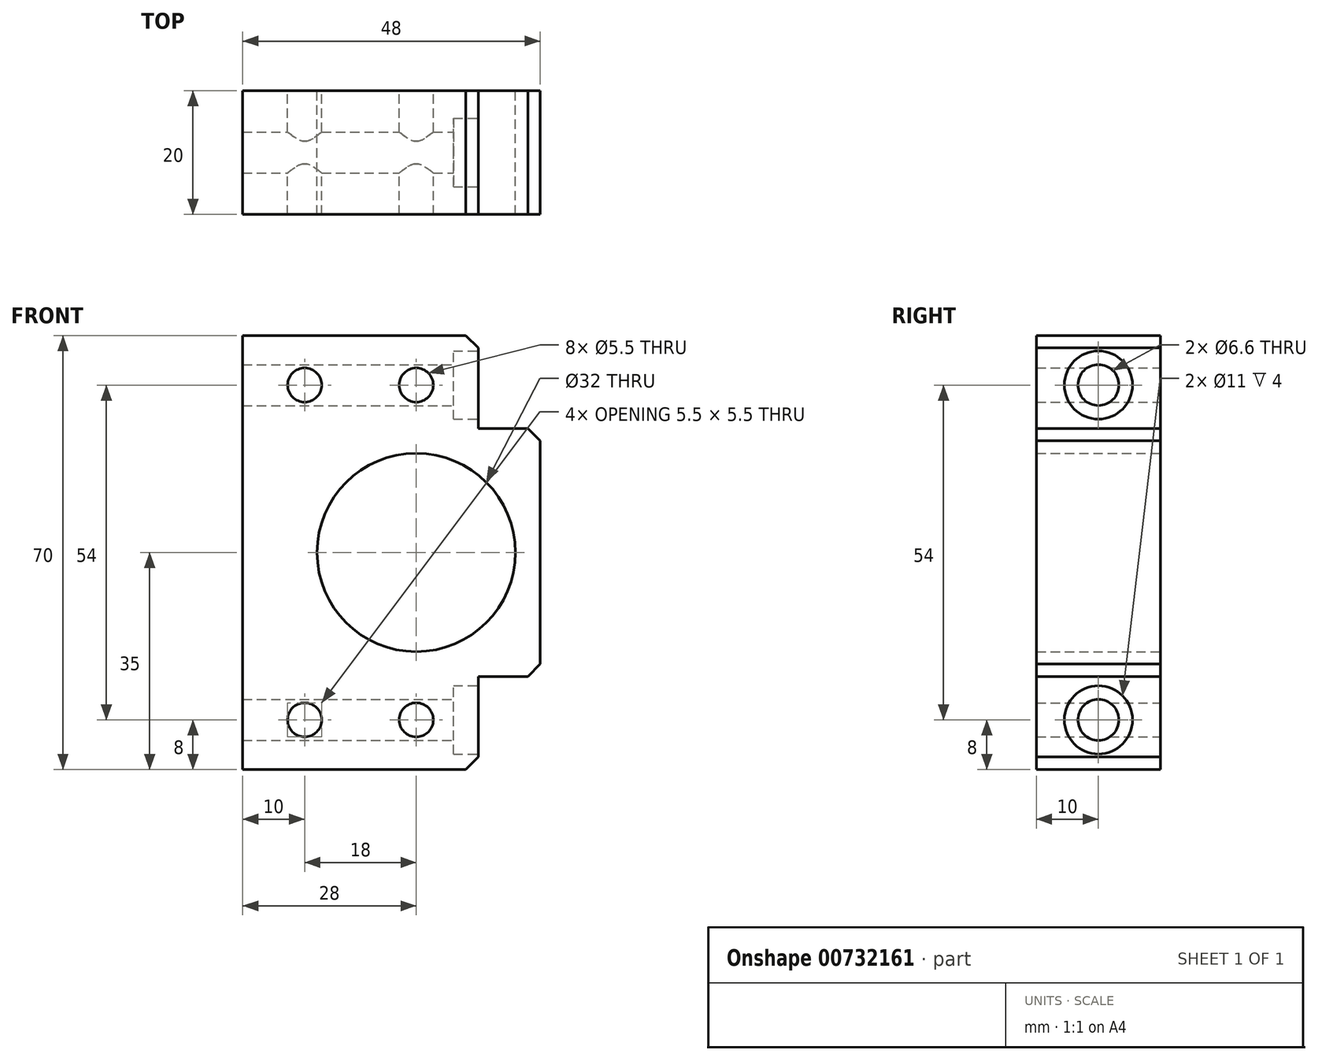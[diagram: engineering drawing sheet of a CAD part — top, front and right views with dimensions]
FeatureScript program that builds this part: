
annotation { "Feature Type Name" : "Feature", "Feature Type Description" : "" }
export const myFeature = defineFeature(function(context is Context, id is Id, definition is map)
    precondition{}
    {
        {
            var Q0;
            Q0=qCreatedBy(makeId("Front.planeOp"),FACE);
            var sketch = newSketch(context, id + "F0", { "sketchPlane" : qUnion([Q0])});
            skLineSegment(sketch, "E0.bottom", {"start": v(0, 0) * mm, "end": v(38, 0) * mm});
            skLineSegment(sketch, "E0.top", {"start": v(0, 70) * mm, "end": v(38, 70) * mm});
            skLineSegment(sketch, "E0.left", {"start": v(0, 0) * mm, "end": v(0, 70) * mm});
            skLineSegment(sketch, "E0.right", {"start": v(48, 15) * mm, "end": v(48, 55) * mm});
            skCircle(sketch, "E1", {"center": v(28, 35) * mm, "radius": 16 * mm});
            skCircle(sketch, "E2", {"center": v(10, 62) * mm, "radius": 2.75 * mm});
            skCircle(sketch, "E3", {"center": v(28, 62) * mm, "radius": 2.75 * mm});
            skCircle(sketch, "E4", {"center": v(10, 8) * mm, "radius": 2.75 * mm});
            skCircle(sketch, "E5", {"center": v(28, 8) * mm, "radius": 2.75 * mm});
            skLineSegment(sketch, "E6.top", {"start": v(48, 55) * mm, "end": v(38, 55) * mm});
            skLineSegment(sketch, "E6.right", {"start": v(38, 70) * mm, "end": v(38, 55) * mm});
            skLineSegment(sketch, "E7.top", {"start": v(48, 15) * mm, "end": v(38, 15) * mm});
            skLineSegment(sketch, "E7.right", {"start": v(38, 0) * mm, "end": v(38, 15) * mm});
            skPoint(sketch, "E6.bottom.start.orphan", {"position": v(48, 70) * mm});
            skSolve(sketch);
        }
        {
            var Q0;
            Q0=makeQuery(id+"F0.imprint","IMPRINT",FACE,{"disambiguationData":[TD([[makeQuery(id+"F0.imprint","IMPRINT",EDGE,{"derivedFrom":sQuery(id+"F0.wireOp",EDGE,"E0.bottom")}),1.0]])]});
            extrude(context, id + "F1", {"entities" : qUnion([Q0]), "depth" : 20 * mm, "offsetDistance" : 25 * mm});
        }
        {
            var Q0;
            Q0=makeQuery(id+"F1.opExtrude","SWEPT_FACE",FACE,{"disambiguationData":[OSD([sQuery(id+"F0.wireOp",EDGE,"E6.right")])]});
            var sketch = newSketch(context, id + "F2", { "sketchPlane" : qUnion([Q0])});
            skCircle(sketch, "E8", {"center": v(-10, 62) * mm, "radius": 3.3 * mm});
            skPoint(sketch, "E8.centerSnap0", {"position": v(-19.48, 62) * mm});
            skCircle(sketch, "E9", {"center": v(-10, 8) * mm, "radius": 3.3 * mm});
            skSolve(sketch);
        }
        {
            var Q0;
            Q0=qSketchRegion(id+"F2",true);
            extrude(context, id + "F3", {"entities" : qUnion([Q0]), "operationType" : NewBodyOperationType.REMOVE, "oppositeDirection" : true, "depth" : 38 * mm, "offsetDistance" : 25 * mm});
        }
        {
            var Q0;
            Q0=makeQuery(id+"F1.opExtrude","SWEPT_FACE",FACE,{"disambiguationData":[OSD([sQuery(id+"F0.wireOp",EDGE,"E6.right")])]});
            var sketch = newSketch(context, id + "F4", { "sketchPlane" : qUnion([Q0])});
            skCircle(sketch, "E10", {"center": v(-10, 62) * mm, "radius": 5.5 * mm});
            skCircle(sketch, "E11", {"center": v(-10, 8) * mm, "radius": 5.5 * mm});
            skSolve(sketch);
        }
        {
            var Q0;
            Q0=qSketchRegion(id+"F4",true);
            extrude(context, id + "F5", {"entities" : qUnion([Q0]), "operationType" : NewBodyOperationType.REMOVE, "oppositeDirection" : true, "depth" : 4 * mm, "offsetDistance" : 25 * mm});
        }
        {
            var Q0;
            Q0=makeQuery(id+"F1.opExtrude","SWEPT_EDGE",EDGE,{"disambiguationData":[OSD([sQuery(id+"F0.wireOp",EDGE,"E0.top"),sQuery(id+"F0.wireOp",EDGE,"E6.right")])]});
            var Q1;
            Q1=makeQuery(id+"F1.opExtrude","SWEPT_EDGE",EDGE,{"disambiguationData":[OSD([sQuery(id+"F0.wireOp",EDGE,"E0.right"),sQuery(id+"F0.wireOp",EDGE,"E6.top")])]});
            var Q2;
            Q2=makeQuery(id+"F1.opExtrude","SWEPT_EDGE",EDGE,{"disambiguationData":[OSD([sQuery(id+"F0.wireOp",EDGE,"E0.bottom"),sQuery(id+"F0.wireOp",EDGE,"E7.right")])]});
            var Q3;
            Q3=makeQuery(id+"F1.opExtrude","SWEPT_EDGE",EDGE,{"disambiguationData":[OSD([sQuery(id+"F0.wireOp",EDGE,"E0.right"),sQuery(id+"F0.wireOp",EDGE,"E7.top")])]});
            chamfer(context, id + "F6", {"entities" : qUnion([Q0, Q1, Q2, Q3]), "width" : 2 * mm, "tangentPropagation" : true});
        }
    });
